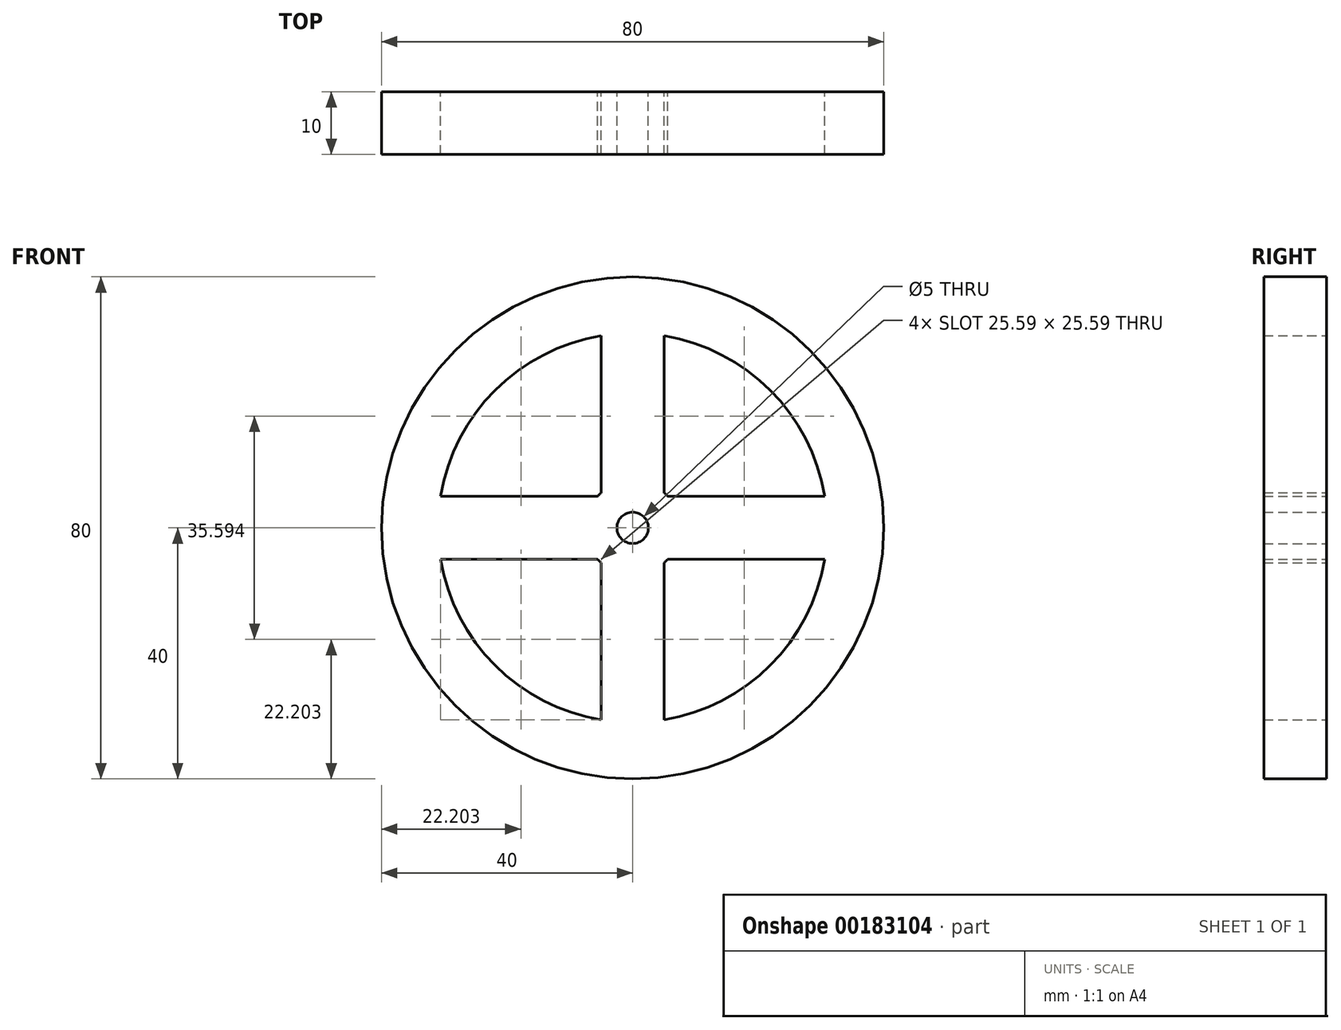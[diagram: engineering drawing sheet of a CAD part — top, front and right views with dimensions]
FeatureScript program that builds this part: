
annotation { "Feature Type Name" : "Feature", "Feature Type Description" : "" }
export const myFeature = defineFeature(function(context is Context, id is Id, definition is map)
    precondition{}
    {
        {
            var Q0;
            Q0=qCreatedBy(makeId("Front.planeOp"),FACE);
            var sketch = newSketch(context, id + "F0", { "sketchPlane" : qUnion([Q0])});
            skCircle(sketch, "E0", {"center": v(0, 0) * mm, "radius": 40 * mm});
            skCircle(sketch, "E1", {"center": v(0, 0) * mm, "radius": 31 * mm});
            skCircle(sketch, "E2", {"center": v(0, 0) * mm, "radius": 7.5 * mm});
            skCircle(sketch, "E3", {"center": v(0, 0) * mm, "radius": 2.5 * mm});
            skLineSegment(sketch, "E4", {"start": v(0, 0) * mm, "end": v(0, 31) * mm});
            skLineSegment(sketch, "E5", {"start": v(0, 0) * mm, "end": v(31, 0) * mm});
            skLineSegment(sketch, "E6", {"start": v(0, 0) * mm, "end": v(0, -31) * mm});
            skLineSegment(sketch, "E7", {"start": v(0, 0) * mm, "end": v(-31, 0) * mm});
            skLineSegment(sketch, "E8.0", {"start": v(5, 5.6) * mm, "end": v(5, 30.6) * mm});
            skLineSegment(sketch, "E9.0", {"start": v(-5, 5.6) * mm, "end": v(-5, 30.6) * mm});
            skLineSegment(sketch, "E10.0", {"start": v(-5.6, 5) * mm, "end": v(-30.6, 5) * mm});
            skLineSegment(sketch, "E11.0", {"start": v(-5.6, -5) * mm, "end": v(-30.6, -5) * mm});
            skLineSegment(sketch, "E12.0", {"start": v(-5, -5.6) * mm, "end": v(-5, -30.6) * mm});
            skLineSegment(sketch, "E13.0", {"start": v(5, -5.6) * mm, "end": v(5, -30.6) * mm});
            skLineSegment(sketch, "E14.0", {"start": v(5.6, -5) * mm, "end": v(30.6, -5) * mm});
            skLineSegment(sketch, "E15.0", {"start": v(5.6, 5) * mm, "end": v(30.6, 5) * mm});
            skLineSegment(sketch, "E16.trimOffspring", {"start": v(39.69, -5) * mm, "end": v(40, -5) * mm});
            skLineSegment(sketch, "E17.trimOffspring", {"start": v(39.69, 5) * mm, "end": v(40, 5) * mm});
            skLineSegment(sketch, "E18.trimOffspring", {"start": v(5, -39.69) * mm, "end": v(5, -40) * mm});
            skLineSegment(sketch, "E19.trimOffspring", {"start": v(-5, -39.69) * mm, "end": v(-5, -40) * mm});
            skLineSegment(sketch, "E20.trimOffspring", {"start": v(-5, 39.69) * mm, "end": v(-5, 40) * mm});
            skLineSegment(sketch, "E21.trimOffspring", {"start": v(5, 39.69) * mm, "end": v(5, 40) * mm});
            skLineSegment(sketch, "E22.trimOffspring", {"start": v(-39.69, 5) * mm, "end": v(-40, 5) * mm});
            skLineSegment(sketch, "E23.trimOffspring", {"start": v(-39.69, -5) * mm, "end": v(-40, -5) * mm});
            skSolve(sketch);
        }
        {
            var Q0;
            {var subQ0=sQuery(id+"F0.wireOp",EDGE,"E9.0");var subQ1=sQuery(id+"F0.wireOp",EDGE,"E0");var subQ2=makeQuery(id+"F0.imprint","INTERSECT",VERTEX,{"derivedFrom":[subQ1,subQ0]});Q0=makeQuery(id+"F0.imprint","IMPRINT",FACE,{"disambiguationData":[TD([[makeQuery(id+"F0.imprint","IMPRINT",EDGE,{"disambiguationData":[TD([[subQ2,-1.0]])],"derivedFrom":subQ1}),1.0]])]});}
            var Q1;
            {var subQ0=sQuery(id+"F0.wireOp",EDGE,"E7");var subQ1=sQuery(id+"F0.wireOp",EDGE,"E0");var subQ2=makeQuery(id+"F0.imprint","INTERSECT",VERTEX,{"derivedFrom":[subQ1,subQ0]});Q1=makeQuery(id+"F0.imprint","IMPRINT",FACE,{"disambiguationData":[TD([[makeQuery(id+"F0.imprint","IMPRINT",EDGE,{"disambiguationData":[TD([[subQ2,1.0]])],"derivedFrom":subQ1}),1.0]])]});}
            var Q2;
            {var subQ0=sQuery(id+"F0.wireOp",EDGE,"E7");var subQ1=sQuery(id+"F0.wireOp",EDGE,"E0");var subQ2=makeQuery(id+"F0.imprint","INTERSECT",VERTEX,{"derivedFrom":[subQ1,subQ0]});Q2=makeQuery(id+"F0.imprint","IMPRINT",FACE,{"disambiguationData":[TD([[makeQuery(id+"F0.imprint","IMPRINT",EDGE,{"disambiguationData":[TD([[subQ2,-1.0]])],"derivedFrom":subQ1}),1.0]])]});}
            var Q3;
            {var subQ0=sQuery(id+"F0.wireOp",EDGE,"E11.0");var subQ1=sQuery(id+"F0.wireOp",EDGE,"E0");var subQ2=makeQuery(id+"F0.imprint","INTERSECT",VERTEX,{"derivedFrom":[subQ1,subQ0]});Q3=makeQuery(id+"F0.imprint","IMPRINT",FACE,{"disambiguationData":[TD([[makeQuery(id+"F0.imprint","IMPRINT",EDGE,{"disambiguationData":[TD([[subQ2,-1.0]])],"derivedFrom":subQ1}),1.0]])]});}
            var Q4;
            {var subQ0=sQuery(id+"F0.wireOp",EDGE,"E6");var subQ1=sQuery(id+"F0.wireOp",EDGE,"E0");var subQ2=makeQuery(id+"F0.imprint","INTERSECT",VERTEX,{"derivedFrom":[subQ1,subQ0]});Q4=makeQuery(id+"F0.imprint","IMPRINT",FACE,{"disambiguationData":[TD([[makeQuery(id+"F0.imprint","IMPRINT",EDGE,{"disambiguationData":[TD([[subQ2,1.0]])],"derivedFrom":subQ1}),1.0]])]});}
            var Q5;
            {var subQ0=sQuery(id+"F0.wireOp",EDGE,"E6");var subQ1=sQuery(id+"F0.wireOp",EDGE,"E0");var subQ2=makeQuery(id+"F0.imprint","INTERSECT",VERTEX,{"derivedFrom":[subQ1,subQ0]});Q5=makeQuery(id+"F0.imprint","IMPRINT",FACE,{"disambiguationData":[TD([[makeQuery(id+"F0.imprint","IMPRINT",EDGE,{"disambiguationData":[TD([[subQ2,-1.0]])],"derivedFrom":subQ1}),1.0]])]});}
            var Q6;
            {var subQ0=sQuery(id+"F0.wireOp",EDGE,"E13.0");var subQ1=sQuery(id+"F0.wireOp",EDGE,"E0");var subQ2=makeQuery(id+"F0.imprint","INTERSECT",VERTEX,{"derivedFrom":[subQ1,subQ0]});Q6=makeQuery(id+"F0.imprint","IMPRINT",FACE,{"disambiguationData":[TD([[makeQuery(id+"F0.imprint","IMPRINT",EDGE,{"disambiguationData":[TD([[subQ2,-1.0]])],"derivedFrom":subQ1}),1.0]])]});}
            var Q7;
            {var subQ0=sQuery(id+"F0.wireOp",EDGE,"E5");var subQ1=sQuery(id+"F0.wireOp",EDGE,"E0");var subQ2=makeQuery(id+"F0.imprint","INTERSECT",VERTEX,{"derivedFrom":[subQ1,subQ0]});Q7=makeQuery(id+"F0.imprint","IMPRINT",FACE,{"disambiguationData":[TD([[makeQuery(id+"F0.imprint","IMPRINT",EDGE,{"disambiguationData":[TD([[subQ2,1.0]])],"derivedFrom":subQ1}),1.0]])]});}
            var Q8;
            {var subQ0=sQuery(id+"F0.wireOp",EDGE,"E5");var subQ1=sQuery(id+"F0.wireOp",EDGE,"E0");var subQ2=makeQuery(id+"F0.imprint","INTERSECT",VERTEX,{"derivedFrom":[subQ1,subQ0]});Q8=makeQuery(id+"F0.imprint","IMPRINT",FACE,{"disambiguationData":[TD([[makeQuery(id+"F0.imprint","IMPRINT",EDGE,{"disambiguationData":[TD([[subQ2,-1.0]])],"derivedFrom":subQ1}),1.0]])]});}
            var Q9;
            {var subQ0=sQuery(id+"F0.wireOp",EDGE,"E15.0");var subQ1=sQuery(id+"F0.wireOp",EDGE,"E0");var subQ2=makeQuery(id+"F0.imprint","INTERSECT",VERTEX,{"derivedFrom":[subQ1,subQ0]});Q9=makeQuery(id+"F0.imprint","IMPRINT",FACE,{"disambiguationData":[TD([[makeQuery(id+"F0.imprint","IMPRINT",EDGE,{"disambiguationData":[TD([[subQ2,-1.0]])],"derivedFrom":subQ1}),1.0]])]});}
            var Q10;
            {var subQ0=sQuery(id+"F0.wireOp",EDGE,"E4");var subQ1=sQuery(id+"F0.wireOp",EDGE,"E0");var subQ2=makeQuery(id+"F0.imprint","INTERSECT",VERTEX,{"derivedFrom":[subQ1,subQ0]});Q10=makeQuery(id+"F0.imprint","IMPRINT",FACE,{"disambiguationData":[TD([[makeQuery(id+"F0.imprint","IMPRINT",EDGE,{"disambiguationData":[TD([[subQ2,1.0]])],"derivedFrom":subQ1}),1.0]])]});}
            var Q11;
            {var subQ0=sQuery(id+"F0.wireOp",EDGE,"E4");var subQ1=sQuery(id+"F0.wireOp",EDGE,"E0");var subQ2=makeQuery(id+"F0.imprint","INTERSECT",VERTEX,{"derivedFrom":[subQ1,subQ0]});Q11=makeQuery(id+"F0.imprint","IMPRINT",FACE,{"disambiguationData":[TD([[makeQuery(id+"F0.imprint","IMPRINT",EDGE,{"disambiguationData":[TD([[subQ2,-1.0]])],"derivedFrom":subQ1}),1.0]])]});}
            var Q12;
            {var subQ0=sQuery(id+"F0.wireOp",EDGE,"E4");var subQ1=sQuery(id+"F0.wireOp",EDGE,"E1");var subQ2=makeQuery(id+"F0.imprint","INTERSECT",VERTEX,{"derivedFrom":[subQ1,subQ0]});Q12=makeQuery(id+"F0.imprint","IMPRINT",FACE,{"disambiguationData":[TD([[makeQuery(id+"F0.imprint","IMPRINT",EDGE,{"disambiguationData":[TD([[subQ2,-1.0]])],"derivedFrom":subQ1}),1.0]])]});}
            var Q13;
            {var subQ0=sQuery(id+"F0.wireOp",EDGE,"E8.0");var subQ1=sQuery(id+"F0.wireOp",EDGE,"E1");var subQ2=makeQuery(id+"F0.imprint","INTERSECT",VERTEX,{"derivedFrom":[subQ1,subQ0]});Q13=makeQuery(id+"F0.imprint","IMPRINT",FACE,{"disambiguationData":[TD([[makeQuery(id+"F0.imprint","IMPRINT",EDGE,{"disambiguationData":[TD([[subQ2,-1.0]])],"derivedFrom":subQ1}),1.0]])]});}
            var Q14;
            {var subQ0=sQuery(id+"F0.wireOp",EDGE,"E5");var subQ1=sQuery(id+"F0.wireOp",EDGE,"E1");var subQ2=makeQuery(id+"F0.imprint","INTERSECT",VERTEX,{"derivedFrom":[subQ1,subQ0]});Q14=makeQuery(id+"F0.imprint","IMPRINT",FACE,{"disambiguationData":[TD([[makeQuery(id+"F0.imprint","IMPRINT",EDGE,{"disambiguationData":[TD([[subQ2,1.0]])],"derivedFrom":subQ1}),1.0]])]});}
            var Q15;
            {var subQ0=sQuery(id+"F0.wireOp",EDGE,"E15.0");var subQ1=sQuery(id+"F0.wireOp",EDGE,"E1");var subQ2=makeQuery(id+"F0.imprint","INTERSECT",VERTEX,{"derivedFrom":[subQ1,subQ0]});Q15=makeQuery(id+"F0.imprint","IMPRINT",FACE,{"disambiguationData":[TD([[makeQuery(id+"F0.imprint","IMPRINT",EDGE,{"disambiguationData":[TD([[subQ2,1.0]])],"derivedFrom":subQ1}),1.0]])]});}
            var Q16;
            {var subQ0=sQuery(id+"F0.wireOp",EDGE,"E6");var subQ1=sQuery(id+"F0.wireOp",EDGE,"E1");var subQ2=makeQuery(id+"F0.imprint","INTERSECT",VERTEX,{"derivedFrom":[subQ1,subQ0]});Q16=makeQuery(id+"F0.imprint","IMPRINT",FACE,{"disambiguationData":[TD([[makeQuery(id+"F0.imprint","IMPRINT",EDGE,{"disambiguationData":[TD([[subQ2,-1.0]])],"derivedFrom":subQ1}),1.0]])]});}
            var Q17;
            {var subQ0=sQuery(id+"F0.wireOp",EDGE,"E12.0");var subQ1=sQuery(id+"F0.wireOp",EDGE,"E1");var subQ2=makeQuery(id+"F0.imprint","INTERSECT",VERTEX,{"derivedFrom":[subQ1,subQ0]});Q17=makeQuery(id+"F0.imprint","IMPRINT",FACE,{"disambiguationData":[TD([[makeQuery(id+"F0.imprint","IMPRINT",EDGE,{"disambiguationData":[TD([[subQ2,-1.0]])],"derivedFrom":subQ1}),1.0]])]});}
            var Q18;
            {var subQ0=sQuery(id+"F0.wireOp",EDGE,"E7");var subQ1=sQuery(id+"F0.wireOp",EDGE,"E1");var subQ2=makeQuery(id+"F0.imprint","INTERSECT",VERTEX,{"derivedFrom":[subQ1,subQ0]});Q18=makeQuery(id+"F0.imprint","IMPRINT",FACE,{"disambiguationData":[TD([[makeQuery(id+"F0.imprint","IMPRINT",EDGE,{"disambiguationData":[TD([[subQ2,-1.0]])],"derivedFrom":subQ1}),1.0]])]});}
            var Q19;
            {var subQ0=sQuery(id+"F0.wireOp",EDGE,"E10.0");var subQ1=sQuery(id+"F0.wireOp",EDGE,"E1");var subQ2=makeQuery(id+"F0.imprint","INTERSECT",VERTEX,{"derivedFrom":[subQ1,subQ0]});Q19=makeQuery(id+"F0.imprint","IMPRINT",FACE,{"disambiguationData":[TD([[makeQuery(id+"F0.imprint","IMPRINT",EDGE,{"disambiguationData":[TD([[subQ2,-1.0]])],"derivedFrom":subQ1}),1.0]])]});}
            var Q20;
            {var subQ0=sQuery(id+"F0.wireOp",EDGE,"E0");var subQ2=makeQuery(id+"F0.imprint","IMPRINT",VERTEX,{"disambiguationData":[OD(1.0)],"derivedFrom":subQ0});Q20=makeQuery(id+"F0.imprint","IMPRINT",FACE,{"disambiguationData":[TD([[makeQuery(id+"F0.imprint","IMPRINT",EDGE,{"disambiguationData":[TD([[subQ2,-1.0]])],"derivedFrom":subQ0}),1.0]])]});}
            var Q21;
            {var subQ5=sQuery(id+"F0.wireOp",EDGE,"E2");var subQ9=makeQuery(id+"F0.imprint","INTERSECT",VERTEX,{"derivedFrom":[subQ5,sQuery(id+"F0.wireOp",EDGE,"E11.0")]});Q21=makeQuery(id+"F0.imprint","IMPRINT",FACE,{"disambiguationData":[TD([[makeQuery(id+"F0.imprint","IMPRINT",EDGE,{"disambiguationData":[TD([[subQ9,1.0]])],"derivedFrom":subQ5}),1.0]])]});}
            var Q22;
            {var subQ5=sQuery(id+"F0.wireOp",EDGE,"E2");var subQ8=makeQuery(id+"F0.imprint","INTERSECT",VERTEX,{"derivedFrom":[subQ5,sQuery(id+"F0.wireOp",EDGE,"E13.0")]});Q22=makeQuery(id+"F0.imprint","IMPRINT",FACE,{"disambiguationData":[TD([[makeQuery(id+"F0.imprint","IMPRINT",EDGE,{"disambiguationData":[TD([[subQ8,1.0]])],"derivedFrom":subQ5}),1.0]])]});}
            var Q23;
            {var subQ5=sQuery(id+"F0.wireOp",EDGE,"E2");var subQ7=makeQuery(id+"F0.imprint","INTERSECT",VERTEX,{"derivedFrom":[subQ5,sQuery(id+"F0.wireOp",EDGE,"E15.0")]});Q23=makeQuery(id+"F0.imprint","IMPRINT",FACE,{"disambiguationData":[TD([[makeQuery(id+"F0.imprint","IMPRINT",EDGE,{"disambiguationData":[TD([[subQ7,1.0]])],"derivedFrom":subQ5}),1.0]])]});}
            var Q24;
            {var subQ0=sQuery(id+"F0.wireOp",EDGE,"E2");var subQ4=makeQuery(id+"F0.imprint","INTERSECT",VERTEX,{"derivedFrom":[subQ0,sQuery(id+"F0.wireOp",EDGE,"E9.0")]});Q24=makeQuery(id+"F0.imprint","IMPRINT",FACE,{"disambiguationData":[TD([[makeQuery(id+"F0.imprint","IMPRINT",EDGE,{"disambiguationData":[TD([[subQ4,1.0]])],"derivedFrom":subQ0}),1.0]])]});}
            extrude(context, id + "F1", {"entities" : qUnion([Q0, Q1, Q2, Q3, Q4, Q5, Q6, Q7, Q8, Q9, Q10, Q11, Q12, Q13, Q14, Q15, Q16, Q17, Q18, Q19, Q20, Q21, Q22, Q23, Q24]), "endBound" : BoundingType.SYMMETRIC, "depth" : 5 * mm});
        }
        {
            var Q0;
            Q0=makeQuery(id+"F1.opExtrude","CAP_FACE",FACE,{"disambiguationData":[OSD([sQuery(id+"F0.wireOp",EDGE,"E0"),sQuery(id+"F0.wireOp",EDGE,"E1"),sQuery(id+"F0.wireOp",EDGE,"E2"),sQuery(id+"F0.wireOp",EDGE,"E8.0"),sQuery(id+"F0.wireOp",EDGE,"E9.0"),sQuery(id+"F0.wireOp",EDGE,"E10.0"),sQuery(id+"F0.wireOp",EDGE,"E11.0"),sQuery(id+"F0.wireOp",EDGE,"E12.0"),sQuery(id+"F0.wireOp",EDGE,"E13.0"),sQuery(id+"F0.wireOp",EDGE,"E14.0"),sQuery(id+"F0.wireOp",EDGE,"E15.0")])],"isStart":true});
            extrude(context, id + "F2", {"entities" : qUnion([Q0]), "operationType" : NewBodyOperationType.ADD, "depth" : 5 * mm});
        }
    });
